# Revit family: RN 91021 Optifitt-Serra-Nippel doppio ridotto
name_source: partatom
category: Rohrformteile
units: mm (PartAtom-declared; Revit-internal decimal feet)

## family parameters
Arbeitsebenenbasiert = Nein
Beim Laden mit Abzugskörper schneiden = Nein
Bemaßung runder Anschluss = Durchmesser verwenden
Gemeinsam genutzt = Nein
Immer vertikal = Ja
Teiletyp = Nicht definiert

## types (5) — shared parameters
1.010.00.2 Blattnummer der Richtlinie = 29
1.010.00.3 Ausgabedatum (Monat) der Richtlinie = 201308
1.010.00.4 Herstellername = R. Nussbaum AG
1.010.00.5 Revisionsdatum der Datei = 20190521
1.010.00.6 Webadresse des Herstellers = http://www.nussbaum.ch
1.100.00.4 Produktbezeichnung = Versorgung
1.110.00.2 Index = 3
1.110.00.4 Produktbezeichnung = Optifitt-Serra
1.960/3L.00.8 Link (URL) = https://www.nussbaum.ch
29.700.00.4 Produktname = Optifitt-Serra-Doppelnippel reduziert, zu Verschraubungen
29.700.00.5 Produktkennung = 2
29.700.00.6 Querschnittsform = 1
29.700.00.7 Nennweitensystem = DN
29.700.00.8 Nenndrucksystem = PN
29.710.02.4 Nenndruck = 16
29.710.02.5 max. zul. Überdruck [hPa] = 1600
29.710.02.7 max. zul. Dauer-Betriebsdruck [hPa] = 1600
29.710.02.9 max. zul. Dauer-Betriebstemperatur [°C] = 90
Connector Visibility = Nein
EnclosingSpace Visibility = Nein
Hersteller = R. Nussbaum AG
URL = https://www.nussbaum.ch

## per-type parameters (varying)
| type | 1.800.00.3 TGA-Nummer | 1.800.00.4 Kommentarfeld | 1.810.00.3 Hersteller-Bestellnummer | 1.810.00.4 DATANORM-Nummer | 1.810.00.6 GTIN-Nummer | 29.710.02.10 Formstück-Gewicht [kg] | 29.710.02.3 Benennung | CONNECTOR0_DIAMETER_dX_0r | CONNECTOR0_dX_01 | CONNECTOR0_ref_dX | CONNECTOR1_DIAMETER_dX_0r | CONNECTOR1_dX_00 | CONNECTOR1_dX_01 | CONNECTOR1_ref_dX | CONNECTOR1_ref_dX2 | Modell | R. Nussbaum AG 91021.72 de Visibility | R. Nussbaum AG 91021.73 de Visibility | R. Nussbaum AG 91021.74 de Visibility | R. Nussbaum AG 91021.75 de Visibility | R. Nussbaum AG 91021.79 de Visibility | Typenkommentare |
| DN=12x20 | 01900300000000000000000000000000000000000000000035000000000000000005 | 91021.79, Optifitt-Serra-Doppelnippel reduziert, zu Verschraubungen, DN=12x20, L=27, R=3/8 | 91021.79 | 91021.79 | 7612945035936 | 0.045 | Optifitt-Serra-Doppelnippel reduziert, zu Verschraubungen, DN=12x20, L=27, R=3/8 | 20 mm | 10 mm  [stored 0.0328084 ft] | 10 mm  [stored 0.0328084 ft] | 10 mm  [stored 0.0328084 ft] | 18 mm | 28 mm | 18 mm | 28 mm | 91021.79 | Nein | Nein | Nein | Nein | Ja | Optifitt-Serra-Nippel doppio ridotto  DN=12x20 |
| DN=20x25 | 01900300000000000000000000000000000000000000000035000000000000000004 | 91021.75, Optifitt-Serra-Doppelnippel reduziert, zu Verschraubungen, DN=20x25, L=35, R=¾ | 91021.75 | 91021.75 | 7612945035912 | 0.092 | Optifitt-Serra-Doppelnippel reduziert, zu Verschraubungen, DN=20x25, L=35, R=¾ | 25 mm  [stored 0.082021 ft] | 17 mm | 17 mm | 20 mm | 23 mm | 35 mm | 23 mm | 35 mm | 91021.75 | Nein | Nein | Nein | Ja | Nein | Optifitt-Serra-Nippel doppio ridotto  DN=20x25 |
| DN=15x25 | 01900300000000000000000000000000000000000000000035000000000000000003 | 91021.74, Optifitt-Serra-Doppelnippel reduziert, zu Verschraubungen, DN=15x25, L=33, R=½ | 91021.74 | 91021.74 | 7612945035905 | 0.087 | Optifitt-Serra-Doppelnippel reduziert, zu Verschraubungen, DN=15x25, L=33, R=½ | 25 mm  [stored 0.082021 ft] | 17 mm | 17 mm | 15 mm | 21 mm | 33 mm | 21 mm | 33 mm | 91021.74 | Nein | Nein | Ja | Nein | Nein | Optifitt-Serra-Nippel doppio ridotto  DN=15x25 |
| DN=15x20 | 01900300000000000000000000000000000000000000000035000000000000000002 | 91021.73, Optifitt-Serra-Doppelnippel reduziert, zu Verschraubungen, DN=15x20, L=31, R=½ | 91021.73 | 91021.73 | 7612945035899 | 0.053 | Optifitt-Serra-Doppelnippel reduziert, zu Verschraubungen, DN=15x20, L=31, R=½ | 20 mm | 10 mm  [stored 0.0328084 ft] | 10 mm  [stored 0.0328084 ft] | 15 mm | 18 mm | 31 mm | 18 mm | 31 mm | 91021.73 | Nein | Ja | Nein | Nein | Nein | Optifitt-Serra-Nippel doppio ridotto  DN=15x20 |
| DN=12x15 | 01900300000000000000000000000000000000000000000035000000000000000001 | 91021.72, Optifitt-Serra-Doppelnippel reduziert, zu Verschraubungen, DN=12x15, L=25, R=3/8 | 91021.72 | 91021.72 | 7612945035882 | 0.033 | Optifitt-Serra-Doppelnippel reduziert, zu Verschraubungen, DN=12x15, L=25, R=3/8 | 15 mm | 9 mm | 9 mm | 10 mm  [stored 0.0328084 ft] | 15 mm | 25 mm  [stored 0.082021 ft] | 15 mm | 25 mm  [stored 0.082021 ft] | 91021.72 | Ja | Nein | Nein | Nein | Nein | Optifitt-Serra-Nippel doppio ridotto  DN=12x15 |

note: [stored X ft] marks values corroborated as IEEE doubles in the binary element streams (Revit-internal decimal feet)

## geometry (parser evidence)
native form markers: Sweep x1
no freeform markers — native parametric forms only
